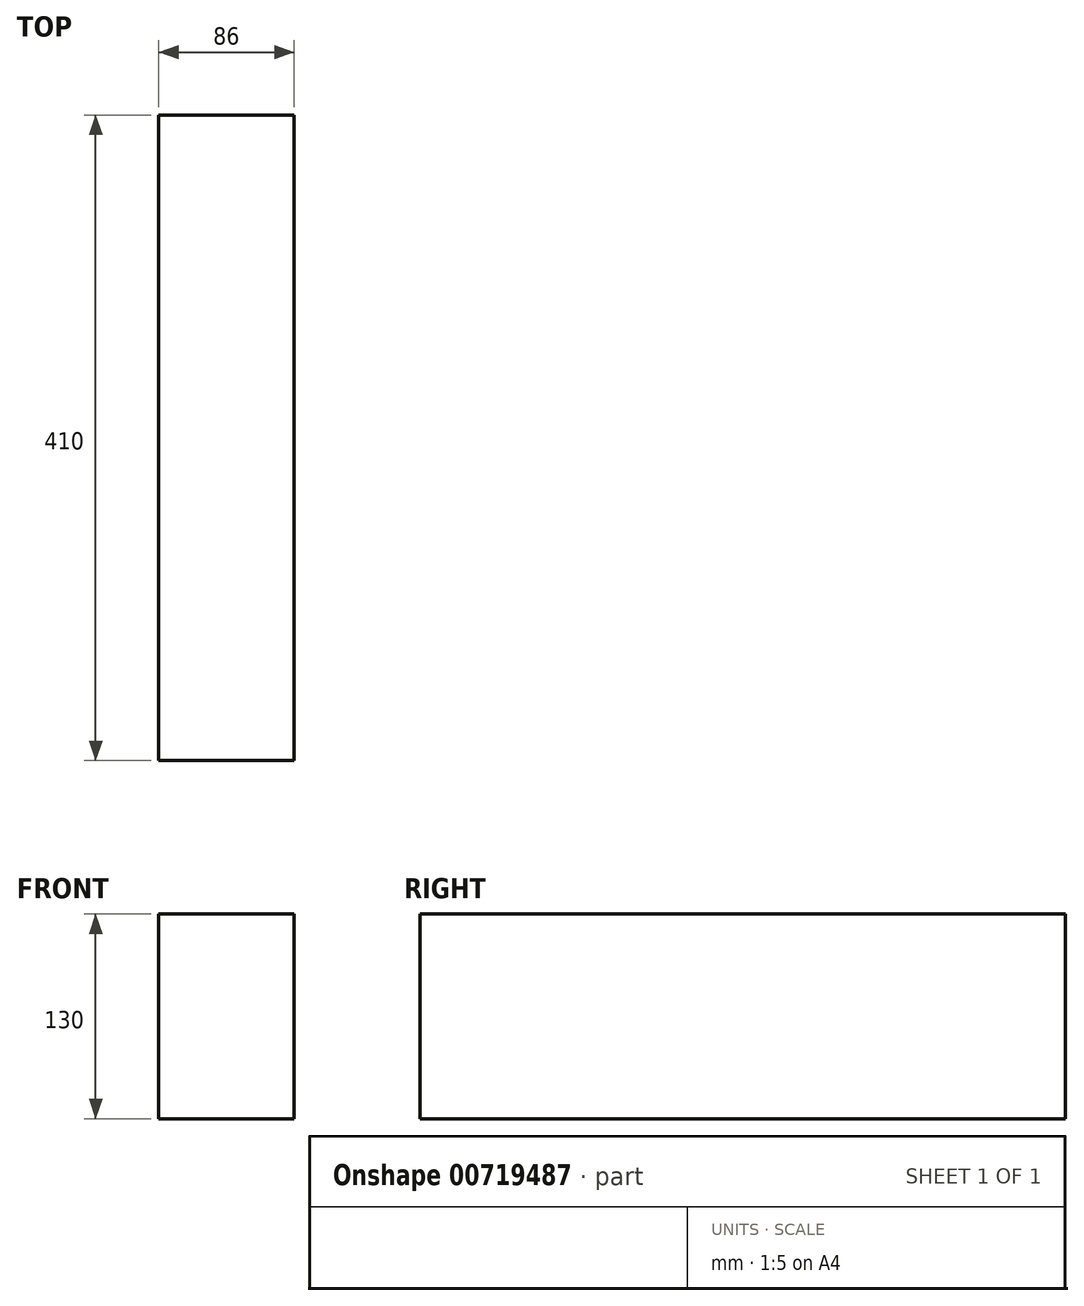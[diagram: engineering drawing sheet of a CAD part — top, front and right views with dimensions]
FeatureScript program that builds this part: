
annotation { "Feature Type Name" : "Feature", "Feature Type Description" : "" }
export const myFeature = defineFeature(function(context is Context, id is Id, definition is map)
    precondition{}
    {
        {
            var Q0;
            Q0=qCreatedBy(makeId("Front.planeOp"),FACE);
            var sketch = newSketch(context, id + "F0", { "sketchPlane" : qUnion([Q0])});
            skLineSegment(sketch, "E0", {"start": v(-43, 0) * mm, "end": v(43, 0) * mm});
            skLineSegment(sketch, "E1", {"start": v(43, 0) * mm, "end": v(43, 130) * mm});
            skLineSegment(sketch, "E2", {"start": v(43, 130) * mm, "end": v(-43, 130) * mm});
            skLineSegment(sketch, "E3", {"start": v(-43, 130) * mm, "end": v(-43, 0) * mm});
            skLineSegment(sketch, "E4", {"start": v(0, 130) * mm, "end": v(0, 0) * mm, "construction": true});
            skSolve(sketch);
        }
        {
            var Q0;
            Q0=makeQuery(id+"F0.imprint","IMPRINT",FACE,{"disambiguationData":[TD([[makeQuery(id+"F0.imprint","IMPRINT",EDGE,{"derivedFrom":sQuery(id+"F0.wireOp",EDGE,"E0")}),1.0]])]});
            extrude(context, id + "F1", {"entities" : qUnion([Q0]), "endBound" : BoundingType.SYMMETRIC, "depth" : 410 * mm, "offsetDistance" : 25 * mm});
        }
    });
